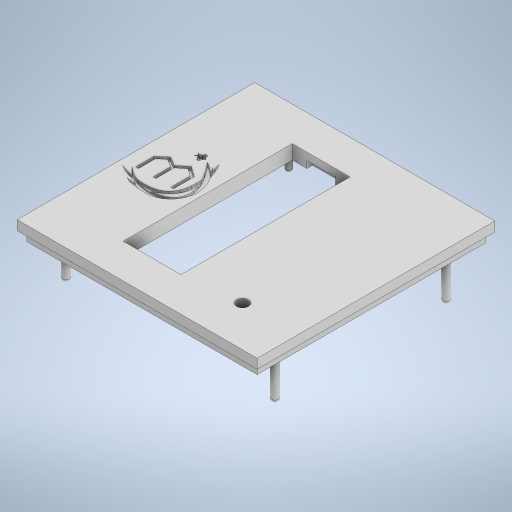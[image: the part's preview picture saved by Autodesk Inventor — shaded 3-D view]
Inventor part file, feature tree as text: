
AUTODESK INVENTOR PART (.ipt)
format: ipt  version: 2023 (Build 270158000, 158)  size: 1,137,664 bytes
history: native  units: mm
features: extrude x13, sketch x8, fillet x2, other x1
ambient origin geometry x8: Origin, YZ Plane, XZ Plane, XY Plane, X Axis, Y Axis, Z Axis, Center Point
bodies: Body1 (feature_tree)
feature tree (24):
  other  "Sólido1"
  extrude  "Base"  Depth=100.0mm
  extrude  "Pinos_encaixe"  Depth=71.15mm
  fillet  "Arredondamento_pino"  Radius=8.0mm
  extrude  "Logo Iobee C.1"  Depth=3.0mm
  extrude  "Logo Iobee C.2"  Depth=3.0mm TaperAngle=0.0deg
  extrude  "Logo Iobee C.3"  Depth=1.5mm TaperAngle=0.0deg
  sketch  "Esboço_ESP32"  dims[d34=28.0mm d35=60.0mm]
  extrude  "ESP32_alocar"  Depth=0.5mm TaperAngle=0.0deg
  extrude  "ESP32_Wi-Fi"  Depth=60.0mm
  extrude  "LCD_Dentro"  Depth=8.0mm
  sketch  "Esboço7"  dims[d2=24.3mm d3=71.15mm d4=8.0mm d5=0.0mm]
  extrude  "Chaveta_LCD"  Depth=4.5mm
  extrude  "LCD Pinos"  Depth=5.0mm TaperAngle=0.0deg
  extrude  "Rasgo de Encaixe"  Depth=3.0mm TaperAngle=0.0deg
  sketch  "Esboço9"  dims[d23=3.0mm d24=3.0mm d25=18.0mm d26=0.0mm]
  extrude  "Pinos Guia LCD"  Depth=36.05mm
  fillet  "Arredondamento2"  Radius=79.9mm
  extrude  "Furo Led"  Depth=2.0mm TaperAngle=0.0deg
  sketch  "Esboço4"  dims[d0=101.0mm d1=100.0mm]
  sketch  "Esboço_LCD_dentro"  dims[d36=19.0mm d37=8.0mm d38=4.5mm d39=5.0mm d40=0.0mm d42=3.0mm d43=0.0mm d44=36.05mm d45=79.9mm d46=2.0mm d47=0.0mm d52=3.0mm d53=0.0mm d54=4.0mm d55=40.0mm d56=6.2mm d57=4.0mm d58=0.0mm d60=4.0mm d61=0.0mm d68=2.5mm d69=2.5mm d70=2.5mm d71=2.5mm d73=75.9mm d74=7.0mm d75=0.0mm d76=1.0mm d77=5.0mm d78=0.0mm d79=0.0mm d80=96.0mm d81=97.0mm d82=6.5mm d83=14.0mm d84=9.2mm d86=32.05mm d88=2.0mm d50=0.5mm d51=0.872665mm]
  sketch  "Esboço8"  dims[d21=3.0mm d22=3.0mm]
  sketch  "Esboço10"  dims[d27=1.5mm d28=1.5mm d29=0.0mm]
  sketch  "Esboço11"  dims[d30=1.0mm d31=0.0mm d32=0.5mm d33=0.0mm]
